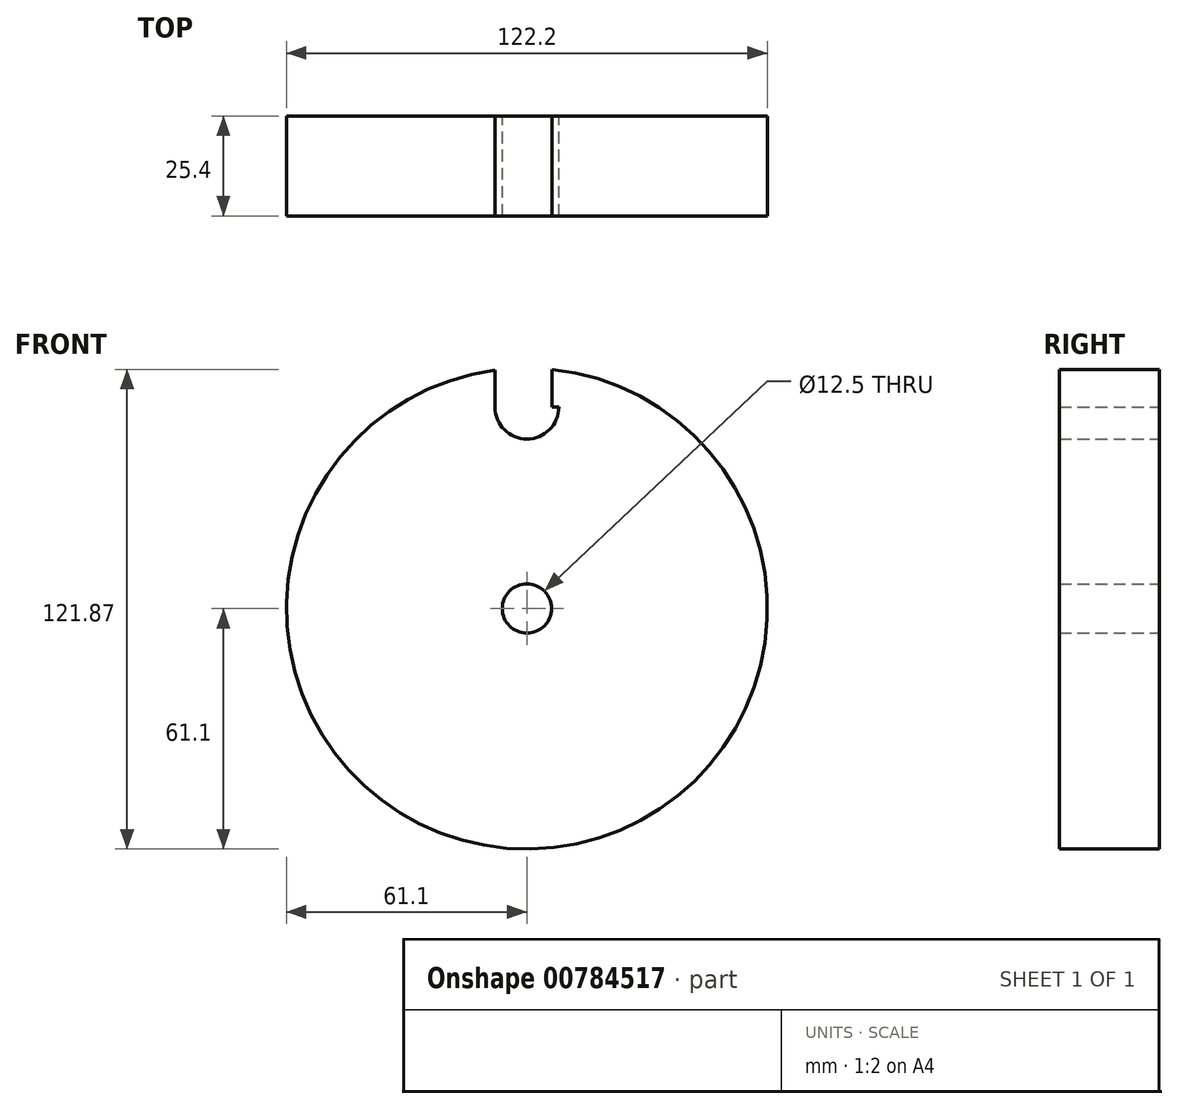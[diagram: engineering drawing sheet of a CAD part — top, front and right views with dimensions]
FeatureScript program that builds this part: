
annotation { "Feature Type Name" : "Feature", "Feature Type Description" : "" }
export const myFeature = defineFeature(function(context is Context, id is Id, definition is map)
    precondition{}
    {
        {
            var Q0;
            Q0=qCreatedBy(makeId("Front.planeOp"),FACE);
            var sketch = newSketch(context, id + "F0", { "sketchPlane" : qUnion([Q0])});
            skCircle(sketch, "E0", {"center": v(0, 0) * mm, "radius": 61.1 * mm});
            skSolve(sketch);
        }
        {
            var Q0;
            Q0 = qSketchRegion(id + "F0", true);
            extrude(context, id + "F1", {"entities" : qUnion([Q0]), "depth" : 25.4 * mm, "offsetDistance" : 25.4 * mm});
        }
        {
            var Q0;
            Q0=qCreatedBy(makeId("Front.planeOp"),FACE);
            var sketch = newSketch(context, id + "F2", { "sketchPlane" : qUnion([Q0])});
            skLineSegment(sketch, "E1", {"start": v(0, 0) * mm, "end": v(0, 11.5) * mm});
            skLineSegment(sketch, "E2", {"start": v(0, 11.5) * mm, "end": v(0, 0) * mm});
            skSolve(sketch);
        }
        {
            var Q0;
            Q0=sQuery(id+"F2.wireOp",VERTEX,"E1.start");
            var Q1;
            Q1=makeQuery(id+"F1.opExtrude","SWEPT_BODY",BODY,{"disambiguationData":[OSD([sQuery(id+"F0.wireOp",EDGE,"E0")])]});
            hole(context, id + "F3", {"style" : HoleStyle.SIMPLE, "endStyle" : HoleEndStyle.THROUGH, "oppositeDirection" : true, "holeDiameter" : 12.5 * mm, "majorDiameter" : 6.35 * mm, "isTappedThrough" : true, "tappedDepth" : 12.7 * mm, "tapClearance" : 3, "locations" : qUnion([Q0]), "scope" : qUnion([Q1])});
        }
        {
            var Q0;
            Q0=makeQuery(id+"F1.opExtrude","CAP_FACE",FACE,{"disambiguationData":[OSD([sQuery(id+"F0.wireOp",EDGE,"E0")])],"isStart":true});
            var sketch = newSketch(context, id + "F4", { "sketchPlane" : qUnion([Q0])});
            skLineSegment(sketch, "E3.top", {"start": v(-8.1, 51.18) * mm, "end": v(-6.4, 51.18) * mm});
            skLineSegment(sketch, "E3.left", {"start": v(-6.4, 60.77) * mm, "end": v(-6.4, 51.18) * mm});
            skLineSegment(sketch, "E3.right", {"start": v(8.1, 60.77) * mm, "end": v(8.1, 51.18) * mm});
            skArc(sketch, "E4", {"start": v(8.1, 51.18) * mm, "mid": v(0, 43.07) * mm, "end": v(-8.1, 51.18) * mm});
            skPoint(sketch, "E4.centerSnap0", {"position": v(0.86, 51.18) * mm});
            skLineSegment(sketch, "E5.trimOffspring", {"start": v(0, 51.18) * mm, "end": v(0.86, 51.18) * mm});
            skArc(sketch, "E6", {"start": v(8.1, 60.77) * mm, "mid": v(0.86, 68.01) * mm, "end": v(-6.4, 60.77) * mm});
            skSolve(sketch);
        }
        {
            var Q0;
            Q0 = qSketchRegion(id + "F4", true);
            extrude(context, id + "F5", {"entities" : qUnion([Q0]), "operationType" : NewBodyOperationType.REMOVE, "oppositeDirection" : true, "depth" : 25.4 * mm, "offsetDistance" : 25.4 * mm});
        }
    });
